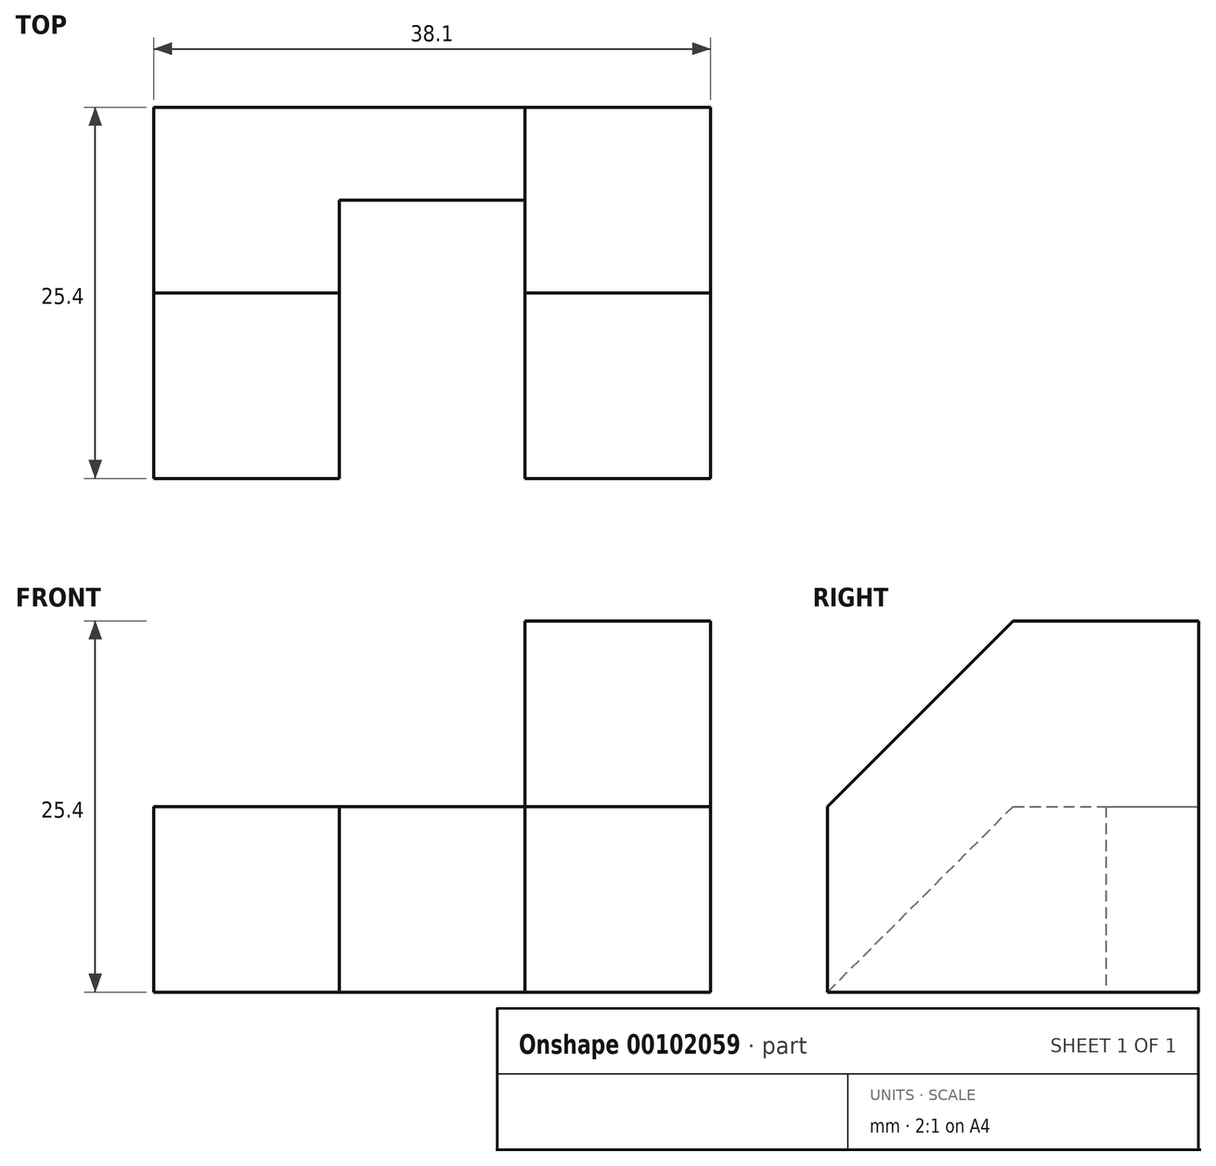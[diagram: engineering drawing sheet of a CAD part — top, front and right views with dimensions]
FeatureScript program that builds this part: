
annotation { "Feature Type Name" : "Feature", "Feature Type Description" : "" }
export const myFeature = defineFeature(function(context is Context, id is Id, definition is map)
    precondition{}
    {
        {
            var Q0;
            Q0=qCreatedBy(makeId("Right.planeOp"),FACE);
            var sketch = newSketch(context, id + "F0", { "sketchPlane" : qUnion([Q0])});
            skLineSegment(sketch, "E0", {"start": v(0, 0) * mm, "end": v(0, 12.7) * mm});
            skLineSegment(sketch, "E1", {"start": v(0, 12.7) * mm, "end": v(12.7, 25.4) * mm});
            skLineSegment(sketch, "E2", {"start": v(12.7, 25.4) * mm, "end": v(25.4, 25.4) * mm});
            skLineSegment(sketch, "E3", {"start": v(25.4, 25.4) * mm, "end": v(25.4, 0) * mm});
            skLineSegment(sketch, "E4", {"start": v(25.4, 0) * mm, "end": v(0, 0) * mm});
            skSolve(sketch);
        }
        {
            var Q0;
            Q0=makeQuery(id+"F0.imprint","IMPRINT",FACE,{"disambiguationData":[TD([[makeQuery(id+"F0.imprint","IMPRINT",EDGE,{"derivedFrom":sQuery(id+"F0.wireOp",EDGE,"E0")}),-1.0]])]});
            extrude(context, id + "F1", {"entities" : qUnion([Q0]), "depth" : 38.1 * mm});
        }
        {
            var Q0;
            Q0=qCreatedBy(makeId("Top.planeOp"),FACE);
            var sketch = newSketch(context, id + "F2", { "sketchPlane" : qUnion([Q0])});
            skLineSegment(sketch, "E5", {"start": v(12.7, 0) * mm, "end": v(12.7, 19.05) * mm});
            skLineSegment(sketch, "E6", {"start": v(12.7, 19.05) * mm, "end": v(25.4, 19.05) * mm});
            skLineSegment(sketch, "E7", {"start": v(25.4, 19.05) * mm, "end": v(25.4, 0) * mm});
            skLineSegment(sketch, "E8", {"start": v(25.4, 0) * mm, "end": v(12.7, 0) * mm});
            skSolve(sketch);
        }
        {
            var Q0;
            Q0 = qSketchRegion(id + "F2", true);
            extrude(context, id + "F3", {"entities" : qUnion([Q0]), "operationType" : NewBodyOperationType.REMOVE, "depth" : 25.4 * mm});
        }
        {
            var Q0;
            Q0=qCreatedBy(makeId("Right.planeOp"),FACE);
            var sketch = newSketch(context, id + "F4", { "sketchPlane" : qUnion([Q0])});
            skLineSegment(sketch, "E9", {"start": v(0, 0) * mm, "end": v(12.7, 12.7) * mm});
            skLineSegment(sketch, "E10", {"start": v(12.7, 12.7) * mm, "end": v(25.4, 12.7) * mm});
            skLineSegment(sketch, "E11", {"start": v(25.4, 12.7) * mm, "end": v(25.4, 25.4) * mm});
            skLineSegment(sketch, "E12", {"start": v(25.4, 25.4) * mm, "end": v(0, 25.4) * mm});
            skLineSegment(sketch, "E13", {"start": v(0, 25.4) * mm, "end": v(0, 0) * mm});
            skSolve(sketch);
        }
        {
            var Q0;
            Q0 = qSketchRegion(id + "F4", true);
            extrude(context, id + "F5", {"entities" : qUnion([Q0]), "operationType" : NewBodyOperationType.REMOVE, "depth" : 25.4 * mm});
        }
    });
